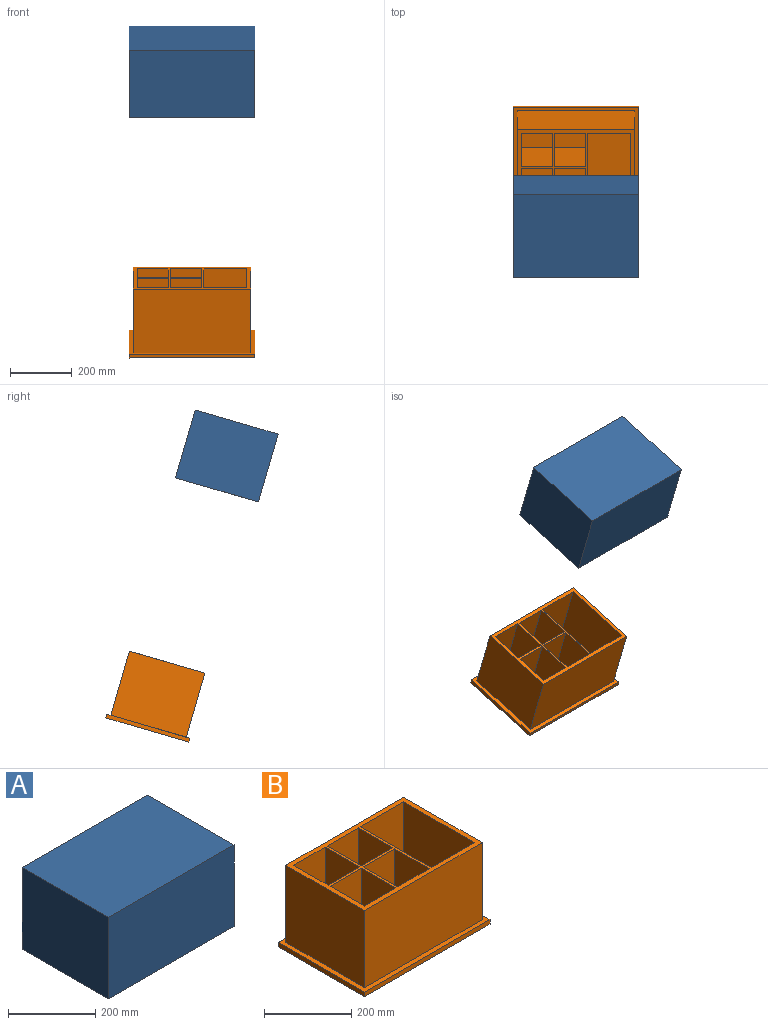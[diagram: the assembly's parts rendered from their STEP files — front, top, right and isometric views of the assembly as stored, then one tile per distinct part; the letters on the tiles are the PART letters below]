
ASSEMBLY  parts=2 mates=1
PART A: 11 faces, bbox 406.4x279.4x228.6 mm
  f0: plane 406.4x279.4mm, normal (0,0,-1), area 8548.4mm2, adj f1,f2,f3,f4,f6,f7,f8,f9
  f1: plane 406.4x228.6mm, normal (0,1,0), area 92903mm2, adj f0,f2,f4,f5
  f2: plane 279.4x228.6mm, normal (-1,0,0), area 63870.8mm2, adj f0,f1,f3,f5
  f3: plane 406.4x228.6mm, normal (0,-1,0), area 92903mm2, adj f0,f2,f4,f5
  f4: plane 279.4x228.6mm, normal (1,0,0), area 63870.8mm2, adj f0,f1,f3,f5
  f5: plane 406.4x279.4mm, normal (0,0,1), area 113548.2mm2, adj f1,f2,f3,f4
  f6: plane 393.7x222.25mm, normal (0,1,0), area 87499.8mm2, adj f0,f7,f9,f10
  f7: plane 266.7x222.25mm, normal (1,0,0), area 59274.1mm2, adj f0,f6,f8,f10
  f8: plane 393.7x222.25mm, normal (0,-1,0), area 87499.8mm2, adj f0,f7,f9,f10
  f9: plane 266.7x222.25mm, normal (-1,0,0), area 59274.1mm2, adj f0,f6,f8,f10
  f10: plane 393.7x266.7mm, normal (0,0,-1), area 104999.8mm2, adj f6,f7,f8,f9
PART B: 36 faces, bbox 406.4x279.4x228.6 mm
  f0: plane 215.9x101.6mm, normal (0,-1,0), area 21935.4mm2, adj f5,f9,f33,f35
  f1: plane 215.9x139.7mm, normal (0,-1,0), area 30161.2mm2, adj f6,f9,f23,f32
  f2: plane 215.9x111.13mm, normal (1,0,0), area 23991.9mm2, adj f9,f22,f24,f27
  f3: plane 215.9x101.6mm, normal (0,1,0), area 21935.4mm2, adj f7,f9,f29,f31
  f4: plane 215.9x139.7mm, normal (0,1,0), area 30161.2mm2, adj f6,f9,f23,f32
  f5: plane 111.13x101.6mm, normal (0,0,1), area 11290.3mm2, adj f0,f33,f34,f35
  f6: plane 228.6x139.7mm, normal (0,0,1), area 31935.4mm2, adj f1,f4,f23,f32
  f7: plane 111.13x101.6mm, normal (0,0,1), area 11290.3mm2, adj f3,f29,f30,f31
  f8: plane 111.13x101.6mm, normal (0,0,1), area 11290.3mm2, adj f20,f21,f25,f26
  f9: plane 381x254mm, normal (0,0,1), area 19677.4mm2, adj f0,f1,f2,f3,f4,f15,f16,f17
  f10: plane 279.4x12.7mm, normal (-1,0,0), area 3548.4mm2, adj f11,f13,f14,f19
  f11: plane 406.4x12.7mm, normal (0,-1,0), area 5161.3mm2, adj f10,f12,f14,f19
  f12: plane 279.4x12.7mm, normal (1,0,0), area 3548.4mm2, adj f11,f13,f14,f19
  f13: plane 406.4x12.7mm, normal (0,1,0), area 5161.3mm2, adj f10,f12,f14,f19
  f14: plane 406.4x279.4mm, normal (0,0,-1), area 113548.2mm2, adj f10,f11,f12,f13
  f15: plane 254x215.9mm, normal (-1,0,0), area 54838.6mm2, adj f9,f16,f18,f19
  f16: plane 381x215.9mm, normal (0,1,0), area 82257.9mm2, adj f9,f15,f17,f19
  f17: plane 254x215.9mm, normal (1,0,0), area 54838.6mm2, adj f9,f16,f18,f19
  f18: plane 381x215.9mm, normal (0,-1,0), area 82257.9mm2, adj f9,f15,f17,f19
  f19: plane 406.4x279.4mm, normal (0,0,1), area 16774.2mm2, adj f10,f11,f12,f13,f15,f16,f17,f18
  f20: plane 215.9x101.6mm, normal (0,-1,0), area 21935.4mm2, adj f8,f9,f21,f25
  f21: plane 215.9x111.13mm, normal (1,0,0), area 23991.9mm2, adj f8,f9,f20,f26
  f22: plane 215.9x101.6mm, normal (0,1,0), area 21935.4mm2, adj f2,f9,f24,f28
  f23: plane 228.6x215.9mm, normal (-1,0,0), area 49354.7mm2, adj f1,f4,f6,f9
  f24: plane 111.13x101.6mm, normal (0,0,1), area 11290.3mm2, adj f2,f22,f27,f28
  f25: plane 215.9x111.13mm, normal (-1,0,0), area 23991.9mm2, adj f8,f9,f20,f26
  f26: plane 215.9x101.6mm, normal (0,1,0), area 21935.4mm2, adj f8,f9,f21,f25
  f27: plane 215.9x101.6mm, normal (0,-1,0), area 21935.4mm2, adj f2,f9,f24,f28
  f28: plane 215.9x111.13mm, normal (-1,0,0), area 23991.9mm2, adj f9,f22,f24,f27
  f29: plane 215.9x111.13mm, normal (1,0,0), area 23991.9mm2, adj f3,f7,f9,f30
  f30: plane 215.9x101.6mm, normal (0,-1,0), area 21935.4mm2, adj f7,f9,f29,f31
  f31: plane 215.9x111.13mm, normal (-1,0,0), area 23991.9mm2, adj f3,f7,f9,f30
  f32: plane 228.6x215.9mm, normal (1,0,0), area 49354.7mm2, adj f1,f4,f6,f9
  f33: plane 215.9x111.13mm, normal (-1,0,0), area 23991.9mm2, adj f0,f5,f9,f34
  f34: plane 215.9x101.6mm, normal (0,1,0), area 21935.4mm2, adj f5,f9,f33,f35
  f35: plane 215.9x111.13mm, normal (1,0,0), area 23991.9mm2, adj f0,f5,f9,f34
PLACE A rot(axis=(1,0,0),16.2deg) t=(555.21,1065.16,-991.66)mm
PLACE B rot(axis=(1,0,0),16.2deg) t=(528.56,1256.37,-1777.71)mm
MATE slider A.f5 <-> B.f14  axis (0,-0.28,0.96) through (614.14,991.76,-774.92)mm
